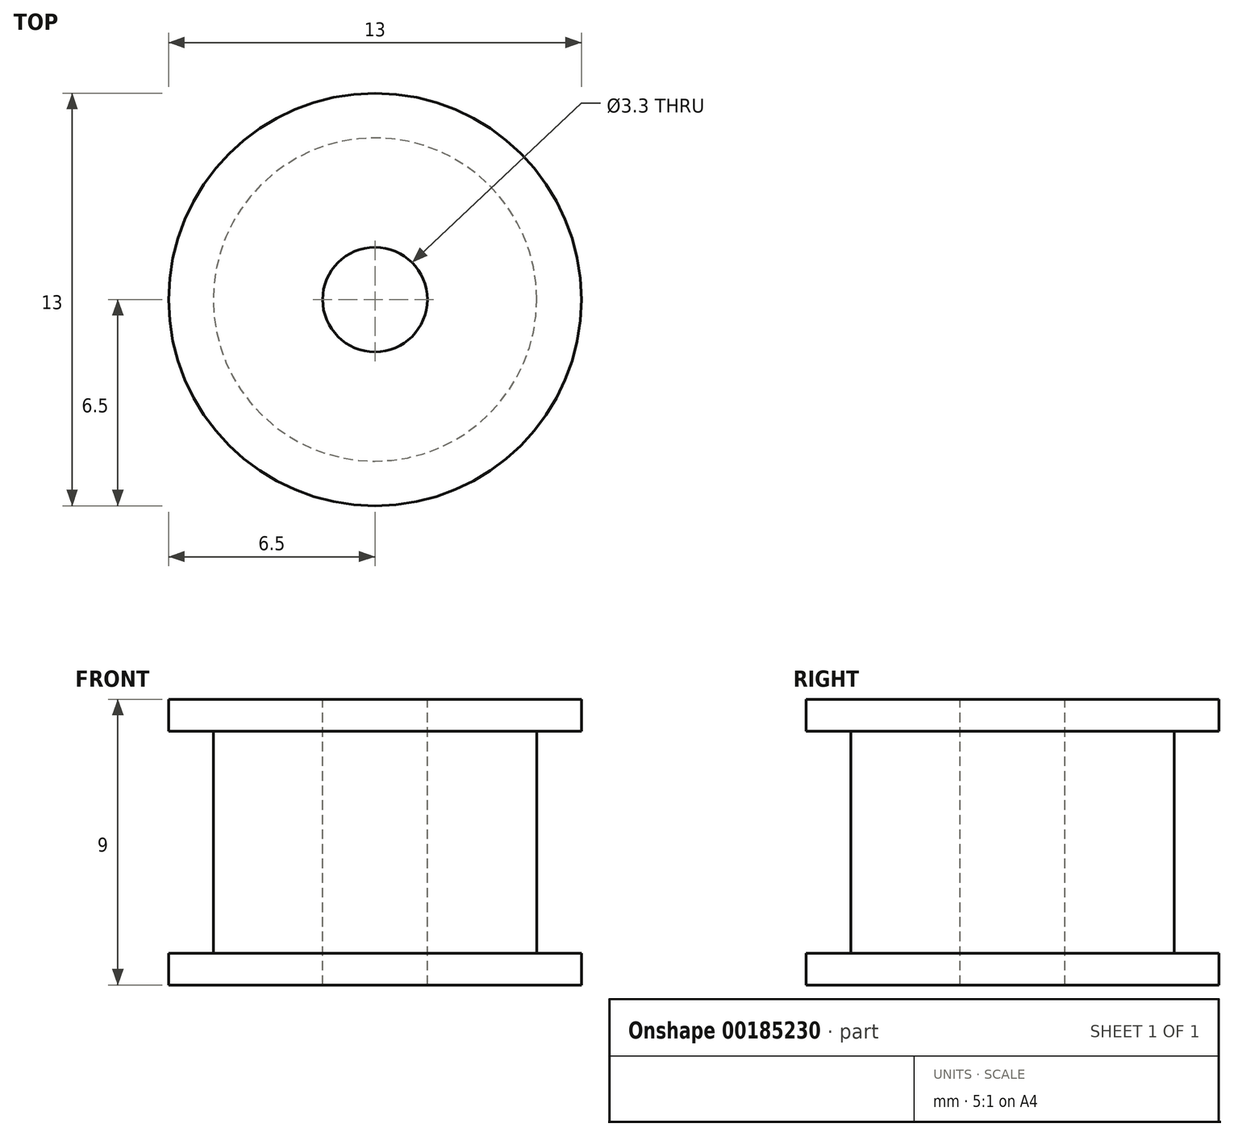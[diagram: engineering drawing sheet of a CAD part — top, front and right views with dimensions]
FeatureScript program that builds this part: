
annotation { "Feature Type Name" : "Feature", "Feature Type Description" : "" }
export const myFeature = defineFeature(function(context is Context, id is Id, definition is map)
    precondition{}
    {
        {
            var Q0;
            Q0=qCreatedBy(makeId("Top.planeOp"),FACE);
            var sketch = newSketch(context, id + "F0", { "sketchPlane" : qUnion([Q0])});
            skPoint(sketch, "E0.center", {"position": v(0, 0) * mm});
            skCircle(sketch, "E1", {"center": v(0, 0) * mm, "radius": 1.65 * mm});
            skCircle(sketch, "E2", {"center": v(0, 0) * mm, "radius": 6.5 * mm});
            skCircle(sketch, "E3", {"center": v(0, 0) * mm, "radius": 5.1 * mm});
            skSolve(sketch);
        }
        {
            var Q0;
            Q0=makeQuery(id+"F0.imprint","IMPRINT",FACE,{"disambiguationData":[TD([[makeQuery(id+"F0.imprint","IMPRINT",EDGE,{"derivedFrom":sQuery(id+"F0.wireOp",EDGE,"E2")}),1.0]])]});
            var Q1;
            Q1=makeQuery(id+"F0.imprint","IMPRINT",FACE,{"disambiguationData":[TD([[makeQuery(id+"F0.imprint","IMPRINT",EDGE,{"derivedFrom":sQuery(id+"F0.wireOp",EDGE,"E1")}),-1.0]])]});
            extrude(context, id + "F1", {"entities" : qUnion([Q0, Q1]), "oppositeDirection" : true, "depth" : 1 * mm});
        }
        {
            var Q0;
            Q0=makeQuery(id+"F0.imprint","IMPRINT",FACE,{"disambiguationData":[TD([[makeQuery(id+"F0.imprint","IMPRINT",EDGE,{"derivedFrom":sQuery(id+"F0.wireOp",EDGE,"e51193dd-6235-4bce-a4e3-aa2c83d8f33c")}),-1.0]])]});
            var Q1;
            Q1=makeQuery(id+"F0.imprint","IMPRINT",FACE,{"disambiguationData":[TD([[makeQuery(id+"F0.imprint","IMPRINT",EDGE,{"derivedFrom":sQuery(id+"F0.wireOp",EDGE,"E1")}),-1.0]])]});
            extrude(context, id + "F2", {"entities" : qUnion([Q0, Q1]), "operationType" : NewBodyOperationType.ADD, "depth" : 7 * mm});
        }
        {
            var Q0;
            Q0=makeQuery(id+"F0.imprint","IMPRINT",FACE,{"disambiguationData":[TD([[makeQuery(id+"F0.imprint","IMPRINT",EDGE,{"derivedFrom":sQuery(id+"F0.wireOp",EDGE,"E1")}),-1.0]])]});
            var Q1;
            Q1=makeQuery(id+"F0.imprint","IMPRINT",FACE,{"disambiguationData":[TD([[makeQuery(id+"F0.imprint","IMPRINT",EDGE,{"derivedFrom":sQuery(id+"F0.wireOp",EDGE,"E2")}),1.0]])]});
            var Q2;
            Q2=makeQuery(id+"F2.opExtrude","CAP_FACE",FACE,{"disambiguationData":[OSD([sQuery(id+"F0.wireOp",EDGE,"e51193dd-6235-4bce-a4e3-aa2c83d8f33c"),sQuery(id+"F0.wireOp",EDGE,"d20b4c91-1525-45e9-8a29-88b2be12989d"),sQuery(id+"F0.wireOp",EDGE,"65c03ec6-645f-4f74-b584-f33019e1610b"),sQuery(id+"F0.wireOp",EDGE,"f0ba81e6-2d7a-4df2-8ac6-a2a38e6fd3f40.MirrorCS"),sQuery(id+"F0.wireOp",EDGE,"01ad706c-fa34-40fa-b4e2-46a727b92d250.MirrorCS"),sQuery(id+"F0.wireOp",EDGE,"f7f77781-9e69-412d-a28a-5a297a567433"),sQuery(id+"F0.wireOp",EDGE,"E0.1.0"),sQuery(id+"F0.wireOp",EDGE,"E0.1.1"),sQuery(id+"F0.wireOp",EDGE,"E0.1.2"),sQuery(id+"F0.wireOp",EDGE,"E0.1.3"),sQuery(id+"F0.wireOp",EDGE,"E0.1.4"),sQuery(id+"F0.wireOp",EDGE,"E0.1.5"),sQuery(id+"F0.wireOp",EDGE,"E0.2.0"),sQuery(id+"F0.wireOp",EDGE,"E0.2.1"),sQuery(id+"F0.wireOp",EDGE,"E0.2.2"),sQuery(id+"F0.wireOp",EDGE,"E0.2.3"),sQuery(id+"F0.wireOp",EDGE,"E0.2.4"),sQuery(id+"F0.wireOp",EDGE,"E0.2.5"),sQuery(id+"F0.wireOp",EDGE,"E0.3.0"),sQuery(id+"F0.wireOp",EDGE,"E0.3.1"),sQuery(id+"F0.wireOp",EDGE,"E0.3.2"),sQuery(id+"F0.wireOp",EDGE,"E0.3.3"),sQuery(id+"F0.wireOp",EDGE,"E0.3.4"),sQuery(id+"F0.wireOp",EDGE,"E0.3.5"),sQuery(id+"F0.wireOp",EDGE,"E0.4.0"),sQuery(id+"F0.wireOp",EDGE,"E0.4.1"),sQuery(id+"F0.wireOp",EDGE,"E0.4.2"),sQuery(id+"F0.wireOp",EDGE,"E0.4.3"),sQuery(id+"F0.wireOp",EDGE,"E0.4.4"),sQuery(id+"F0.wireOp",EDGE,"E0.4.5"),sQuery(id+"F0.wireOp",EDGE,"E0.5.0"),sQuery(id+"F0.wireOp",EDGE,"E0.5.1"),sQuery(id+"F0.wireOp",EDGE,"E0.5.2"),sQuery(id+"F0.wireOp",EDGE,"E0.5.3"),sQuery(id+"F0.wireOp",EDGE,"E0.5.4"),sQuery(id+"F0.wireOp",EDGE,"E0.5.5"),sQuery(id+"F0.wireOp",EDGE,"E0.6.0"),sQuery(id+"F0.wireOp",EDGE,"E0.6.1"),sQuery(id+"F0.wireOp",EDGE,"E0.6.2"),sQuery(id+"F0.wireOp",EDGE,"E0.6.3"),sQuery(id+"F0.wireOp",EDGE,"E0.6.4"),sQuery(id+"F0.wireOp",EDGE,"E0.6.5"),sQuery(id+"F0.wireOp",EDGE,"E0.7.0"),sQuery(id+"F0.wireOp",EDGE,"E0.7.1"),sQuery(id+"F0.wireOp",EDGE,"E0.7.2"),sQuery(id+"F0.wireOp",EDGE,"E0.7.3"),sQuery(id+"F0.wireOp",EDGE,"E0.7.4"),sQuery(id+"F0.wireOp",EDGE,"E0.7.5"),sQuery(id+"F0.wireOp",EDGE,"E0.8.0"),sQuery(id+"F0.wireOp",EDGE,"E0.8.1"),sQuery(id+"F0.wireOp",EDGE,"E0.8.2"),sQuery(id+"F0.wireOp",EDGE,"E0.8.3"),sQuery(id+"F0.wireOp",EDGE,"E0.8.4"),sQuery(id+"F0.wireOp",EDGE,"E0.8.5"),sQuery(id+"F0.wireOp",EDGE,"E0.9.0"),sQuery(id+"F0.wireOp",EDGE,"E0.9.1"),sQuery(id+"F0.wireOp",EDGE,"E0.9.2"),sQuery(id+"F0.wireOp",EDGE,"E0.9.3"),sQuery(id+"F0.wireOp",EDGE,"E0.9.4"),sQuery(id+"F0.wireOp",EDGE,"E0.9.5"),sQuery(id+"F0.wireOp",EDGE,"E0.10.0"),sQuery(id+"F0.wireOp",EDGE,"E0.10.1"),sQuery(id+"F0.wireOp",EDGE,"E0.10.2"),sQuery(id+"F0.wireOp",EDGE,"E0.10.3"),sQuery(id+"F0.wireOp",EDGE,"E0.10.4"),sQuery(id+"F0.wireOp",EDGE,"E0.10.5"),sQuery(id+"F0.wireOp",EDGE,"E0.11.0"),sQuery(id+"F0.wireOp",EDGE,"E0.11.1"),sQuery(id+"F0.wireOp",EDGE,"E0.11.2"),sQuery(id+"F0.wireOp",EDGE,"E0.11.3"),sQuery(id+"F0.wireOp",EDGE,"E0.11.4"),sQuery(id+"F0.wireOp",EDGE,"E0.11.5"),sQuery(id+"F0.wireOp",EDGE,"E0.12.0"),sQuery(id+"F0.wireOp",EDGE,"E0.12.1"),sQuery(id+"F0.wireOp",EDGE,"E0.12.2"),sQuery(id+"F0.wireOp",EDGE,"E0.12.3"),sQuery(id+"F0.wireOp",EDGE,"E0.12.4"),sQuery(id+"F0.wireOp",EDGE,"E0.12.5"),sQuery(id+"F0.wireOp",EDGE,"E0.13.0"),sQuery(id+"F0.wireOp",EDGE,"E0.13.1"),sQuery(id+"F0.wireOp",EDGE,"E0.13.2"),sQuery(id+"F0.wireOp",EDGE,"E0.13.3"),sQuery(id+"F0.wireOp",EDGE,"E0.13.4"),sQuery(id+"F0.wireOp",EDGE,"E0.13.5"),sQuery(id+"F0.wireOp",EDGE,"E0.14.0"),sQuery(id+"F0.wireOp",EDGE,"E0.14.1"),sQuery(id+"F0.wireOp",EDGE,"E0.14.2"),sQuery(id+"F0.wireOp",EDGE,"E0.14.3"),sQuery(id+"F0.wireOp",EDGE,"E0.14.4"),sQuery(id+"F0.wireOp",EDGE,"E0.14.5"),sQuery(id+"F0.wireOp",EDGE,"E0.15.0"),sQuery(id+"F0.wireOp",EDGE,"E0.15.1"),sQuery(id+"F0.wireOp",EDGE,"E0.15.2"),sQuery(id+"F0.wireOp",EDGE,"E0.15.3"),sQuery(id+"F0.wireOp",EDGE,"E0.15.4"),sQuery(id+"F0.wireOp",EDGE,"E0.15.5"),sQuery(id+"F0.wireOp",EDGE,"E1")])],"isStart":false});
            var Q3;
            Q3=makeQuery(id+"F2.opExtrude","CAP_FACE",FACE,{"disambiguationData":[OSD([sQuery(id+"F0.wireOp",EDGE,"e51193dd-6235-4bce-a4e3-aa2c83d8f33c"),sQuery(id+"F0.wireOp",EDGE,"d20b4c91-1525-45e9-8a29-88b2be12989d"),sQuery(id+"F0.wireOp",EDGE,"65c03ec6-645f-4f74-b584-f33019e1610b"),sQuery(id+"F0.wireOp",EDGE,"f0ba81e6-2d7a-4df2-8ac6-a2a38e6fd3f40.MirrorCS"),sQuery(id+"F0.wireOp",EDGE,"01ad706c-fa34-40fa-b4e2-46a727b92d250.MirrorCS"),sQuery(id+"F0.wireOp",EDGE,"f7f77781-9e69-412d-a28a-5a297a567433"),sQuery(id+"F0.wireOp",EDGE,"E0.1.0"),sQuery(id+"F0.wireOp",EDGE,"E0.1.1"),sQuery(id+"F0.wireOp",EDGE,"E0.1.2"),sQuery(id+"F0.wireOp",EDGE,"E0.1.3"),sQuery(id+"F0.wireOp",EDGE,"E0.1.4"),sQuery(id+"F0.wireOp",EDGE,"E0.1.5"),sQuery(id+"F0.wireOp",EDGE,"E0.2.0"),sQuery(id+"F0.wireOp",EDGE,"E0.2.1"),sQuery(id+"F0.wireOp",EDGE,"E0.2.2"),sQuery(id+"F0.wireOp",EDGE,"E0.2.3"),sQuery(id+"F0.wireOp",EDGE,"E0.2.4"),sQuery(id+"F0.wireOp",EDGE,"E0.2.5"),sQuery(id+"F0.wireOp",EDGE,"E0.3.0"),sQuery(id+"F0.wireOp",EDGE,"E0.3.1"),sQuery(id+"F0.wireOp",EDGE,"E0.3.2"),sQuery(id+"F0.wireOp",EDGE,"E0.3.3"),sQuery(id+"F0.wireOp",EDGE,"E0.3.4"),sQuery(id+"F0.wireOp",EDGE,"E0.3.5"),sQuery(id+"F0.wireOp",EDGE,"E0.4.0"),sQuery(id+"F0.wireOp",EDGE,"E0.4.1"),sQuery(id+"F0.wireOp",EDGE,"E0.4.2"),sQuery(id+"F0.wireOp",EDGE,"E0.4.3"),sQuery(id+"F0.wireOp",EDGE,"E0.4.4"),sQuery(id+"F0.wireOp",EDGE,"E0.4.5"),sQuery(id+"F0.wireOp",EDGE,"E0.5.0"),sQuery(id+"F0.wireOp",EDGE,"E0.5.1"),sQuery(id+"F0.wireOp",EDGE,"E0.5.2"),sQuery(id+"F0.wireOp",EDGE,"E0.5.3"),sQuery(id+"F0.wireOp",EDGE,"E0.5.4"),sQuery(id+"F0.wireOp",EDGE,"E0.5.5"),sQuery(id+"F0.wireOp",EDGE,"E0.6.0"),sQuery(id+"F0.wireOp",EDGE,"E0.6.1"),sQuery(id+"F0.wireOp",EDGE,"E0.6.2"),sQuery(id+"F0.wireOp",EDGE,"E0.6.3"),sQuery(id+"F0.wireOp",EDGE,"E0.6.4"),sQuery(id+"F0.wireOp",EDGE,"E0.6.5"),sQuery(id+"F0.wireOp",EDGE,"E0.7.0"),sQuery(id+"F0.wireOp",EDGE,"E0.7.1"),sQuery(id+"F0.wireOp",EDGE,"E0.7.2"),sQuery(id+"F0.wireOp",EDGE,"E0.7.3"),sQuery(id+"F0.wireOp",EDGE,"E0.7.4"),sQuery(id+"F0.wireOp",EDGE,"E0.7.5"),sQuery(id+"F0.wireOp",EDGE,"E0.8.0"),sQuery(id+"F0.wireOp",EDGE,"E0.8.1"),sQuery(id+"F0.wireOp",EDGE,"E0.8.2"),sQuery(id+"F0.wireOp",EDGE,"E0.8.3"),sQuery(id+"F0.wireOp",EDGE,"E0.8.4"),sQuery(id+"F0.wireOp",EDGE,"E0.8.5"),sQuery(id+"F0.wireOp",EDGE,"E0.9.0"),sQuery(id+"F0.wireOp",EDGE,"E0.9.1"),sQuery(id+"F0.wireOp",EDGE,"E0.9.2"),sQuery(id+"F0.wireOp",EDGE,"E0.9.3"),sQuery(id+"F0.wireOp",EDGE,"E0.9.4"),sQuery(id+"F0.wireOp",EDGE,"E0.9.5"),sQuery(id+"F0.wireOp",EDGE,"E0.10.0"),sQuery(id+"F0.wireOp",EDGE,"E0.10.1"),sQuery(id+"F0.wireOp",EDGE,"E0.10.2"),sQuery(id+"F0.wireOp",EDGE,"E0.10.3"),sQuery(id+"F0.wireOp",EDGE,"E0.10.4"),sQuery(id+"F0.wireOp",EDGE,"E0.10.5"),sQuery(id+"F0.wireOp",EDGE,"E0.11.0"),sQuery(id+"F0.wireOp",EDGE,"E0.11.1"),sQuery(id+"F0.wireOp",EDGE,"E0.11.2"),sQuery(id+"F0.wireOp",EDGE,"E0.11.3"),sQuery(id+"F0.wireOp",EDGE,"E0.11.4"),sQuery(id+"F0.wireOp",EDGE,"E0.11.5"),sQuery(id+"F0.wireOp",EDGE,"E0.12.0"),sQuery(id+"F0.wireOp",EDGE,"E0.12.1"),sQuery(id+"F0.wireOp",EDGE,"E0.12.2"),sQuery(id+"F0.wireOp",EDGE,"E0.12.3"),sQuery(id+"F0.wireOp",EDGE,"E0.12.4"),sQuery(id+"F0.wireOp",EDGE,"E0.12.5"),sQuery(id+"F0.wireOp",EDGE,"E0.13.0"),sQuery(id+"F0.wireOp",EDGE,"E0.13.1"),sQuery(id+"F0.wireOp",EDGE,"E0.13.2"),sQuery(id+"F0.wireOp",EDGE,"E0.13.3"),sQuery(id+"F0.wireOp",EDGE,"E0.13.4"),sQuery(id+"F0.wireOp",EDGE,"E0.13.5"),sQuery(id+"F0.wireOp",EDGE,"E0.14.0"),sQuery(id+"F0.wireOp",EDGE,"E0.14.1"),sQuery(id+"F0.wireOp",EDGE,"E0.14.2"),sQuery(id+"F0.wireOp",EDGE,"E0.14.3"),sQuery(id+"F0.wireOp",EDGE,"E0.14.4"),sQuery(id+"F0.wireOp",EDGE,"E0.14.5"),sQuery(id+"F0.wireOp",EDGE,"E0.15.0"),sQuery(id+"F0.wireOp",EDGE,"E0.15.1"),sQuery(id+"F0.wireOp",EDGE,"E0.15.2"),sQuery(id+"F0.wireOp",EDGE,"E0.15.3"),sQuery(id+"F0.wireOp",EDGE,"E0.15.4"),sQuery(id+"F0.wireOp",EDGE,"E0.15.5"),sQuery(id+"F0.wireOp",EDGE,"E1")])],"isStart":false});
            extrude(context, id + "F3", {"entities" : qUnion([Q0, Q1]), "operationType" : NewBodyOperationType.ADD, "endBoundEntityFace" : qUnion([Q2]), "depth" : 8 * mm, "hasSecondDirection" : true, "secondDirectionBound" : SecondDirectionBoundingType.UP_TO_SURFACE, "secondDirectionOppositeDirection" : false, "secondDirectionBoundEntityFace" : qUnion([Q3]), "secondDirectionDepth" : 8 * mm});
        }
    });
